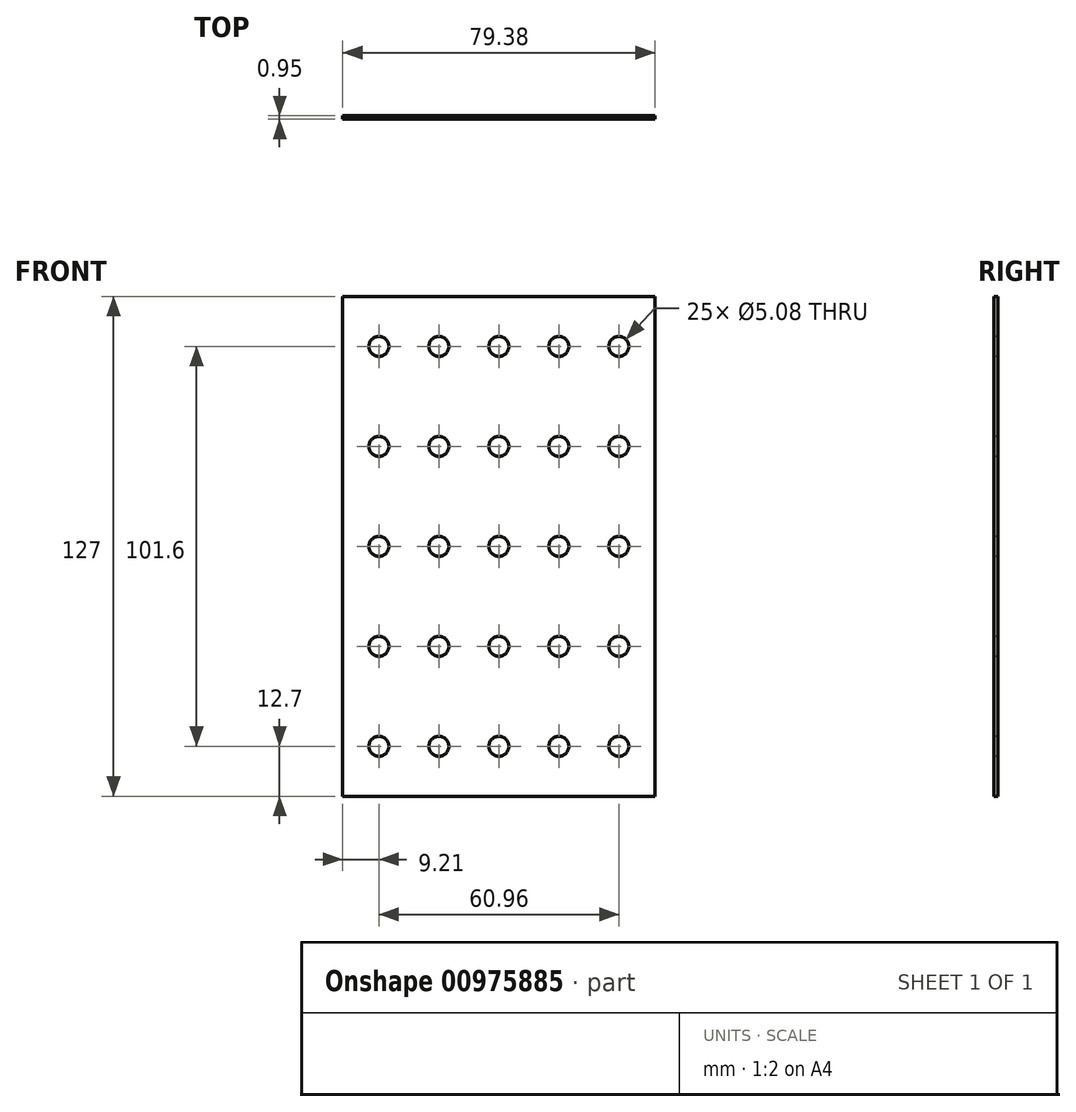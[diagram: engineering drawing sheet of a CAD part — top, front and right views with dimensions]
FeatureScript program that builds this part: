
annotation { "Feature Type Name" : "Feature", "Feature Type Description" : "" }
export const myFeature = defineFeature(function(context is Context, id is Id, definition is map)
    precondition{}
    {
        {
            var Q0;
            Q0=qCreatedBy(makeId("Front.planeOp"),FACE);
            var sketch = newSketch(context, id + "F0", { "sketchPlane" : qUnion([Q0])});
            skLineSegment(sketch, "E0.bottom", {"start": v(39.69, 63.5) * mm, "end": v(-39.69, 63.5) * mm});
            skLineSegment(sketch, "E0.top", {"start": v(39.69, -63.5) * mm, "end": v(-39.69, -63.5) * mm});
            skLineSegment(sketch, "E0.left", {"start": v(39.69, 63.5) * mm, "end": v(39.69, -63.5) * mm});
            skLineSegment(sketch, "E0.right", {"start": v(-39.69, 63.5) * mm, "end": v(-39.69, -63.5) * mm});
            skPoint(sketch, "E0.middle", {"position": v(0, 0) * mm});
            skCircle(sketch, "E1", {"center": v(-30.48, 50.8) * mm, "radius": 2.54 * mm});
            skCircle(sketch, "E2.0.1.0", {"center": v(-30.48, 25.4) * mm, "radius": 2.54 * mm});
            skCircle(sketch, "E2.0.2.0", {"center": v(-30.48, 0) * mm, "radius": 2.54 * mm});
            skCircle(sketch, "E2.0.3.0", {"center": v(-30.48, -25.4) * mm, "radius": 2.54 * mm});
            skCircle(sketch, "E2.0.4.0", {"center": v(-30.48, -50.8) * mm, "radius": 2.54 * mm});
            skCircle(sketch, "E2.1.0.0", {"center": v(-15.24, 50.8) * mm, "radius": 2.54 * mm});
            skCircle(sketch, "E2.1.1.0", {"center": v(-15.24, 25.4) * mm, "radius": 2.54 * mm});
            skCircle(sketch, "E2.1.2.0", {"center": v(-15.24, 0) * mm, "radius": 2.54 * mm});
            skCircle(sketch, "E2.1.3.0", {"center": v(-15.24, -25.4) * mm, "radius": 2.54 * mm});
            skCircle(sketch, "E2.1.4.0", {"center": v(-15.24, -50.8) * mm, "radius": 2.54 * mm});
            skCircle(sketch, "E2.2.0.0", {"center": v(0, 50.8) * mm, "radius": 2.54 * mm});
            skCircle(sketch, "E2.2.1.0", {"center": v(0, 25.4) * mm, "radius": 2.54 * mm});
            skCircle(sketch, "E2.2.2.0", {"center": v(0, 0) * mm, "radius": 2.54 * mm});
            skCircle(sketch, "E2.2.3.0", {"center": v(0, -25.4) * mm, "radius": 2.54 * mm});
            skCircle(sketch, "E2.2.4.0", {"center": v(0, -50.8) * mm, "radius": 2.54 * mm});
            skLineSegment(sketch, "E2.direction1", {"start": v(-30.48, 50.8) * mm, "end": v(-15.24, 50.8) * mm, "construction": true});
            skLineSegment(sketch, "E2.direction2", {"start": v(-30.48, 50.8) * mm, "end": v(-30.48, 25.4) * mm, "construction": true});
            skCircle(sketch, "E3.0.3.0", {"center": v(15.24, 50.8) * mm, "radius": 2.54 * mm});
            skCircle(sketch, "E3.0.3.1", {"center": v(15.24, 25.4) * mm, "radius": 2.54 * mm});
            skCircle(sketch, "E3.0.3.2", {"center": v(15.24, 0) * mm, "radius": 2.54 * mm});
            skCircle(sketch, "E3.0.3.3", {"center": v(15.24, -25.4) * mm, "radius": 2.54 * mm});
            skCircle(sketch, "E3.0.3.4", {"center": v(15.24, -50.8) * mm, "radius": 2.54 * mm});
            skCircle(sketch, "E3.0.4.0", {"center": v(30.48, 50.8) * mm, "radius": 2.54 * mm});
            skCircle(sketch, "E3.0.4.1", {"center": v(30.48, 25.4) * mm, "radius": 2.54 * mm});
            skCircle(sketch, "E3.0.4.2", {"center": v(30.48, 0) * mm, "radius": 2.54 * mm});
            skCircle(sketch, "E3.0.4.3", {"center": v(30.48, -25.4) * mm, "radius": 2.54 * mm});
            skCircle(sketch, "E3.0.4.4", {"center": v(30.48, -50.8) * mm, "radius": 2.54 * mm});
            skSolve(sketch);
        }
        {
            var Q0;
            Q0=makeQuery(id+"F0.imprint","IMPRINT",FACE,{"disambiguationData":[TD([[makeQuery(id+"F0.imprint","IMPRINT",EDGE,{"derivedFrom":sQuery(id+"F0.wireOp",EDGE,"E0.bottom")}),1.0]])]});
            extrude(context, id + "F1", {"entities" : qUnion([Q0]), "oppositeDirection" : true, "depth" : 0.95 * mm, "offsetDistance" : 25.4 * mm});
        }
    });
